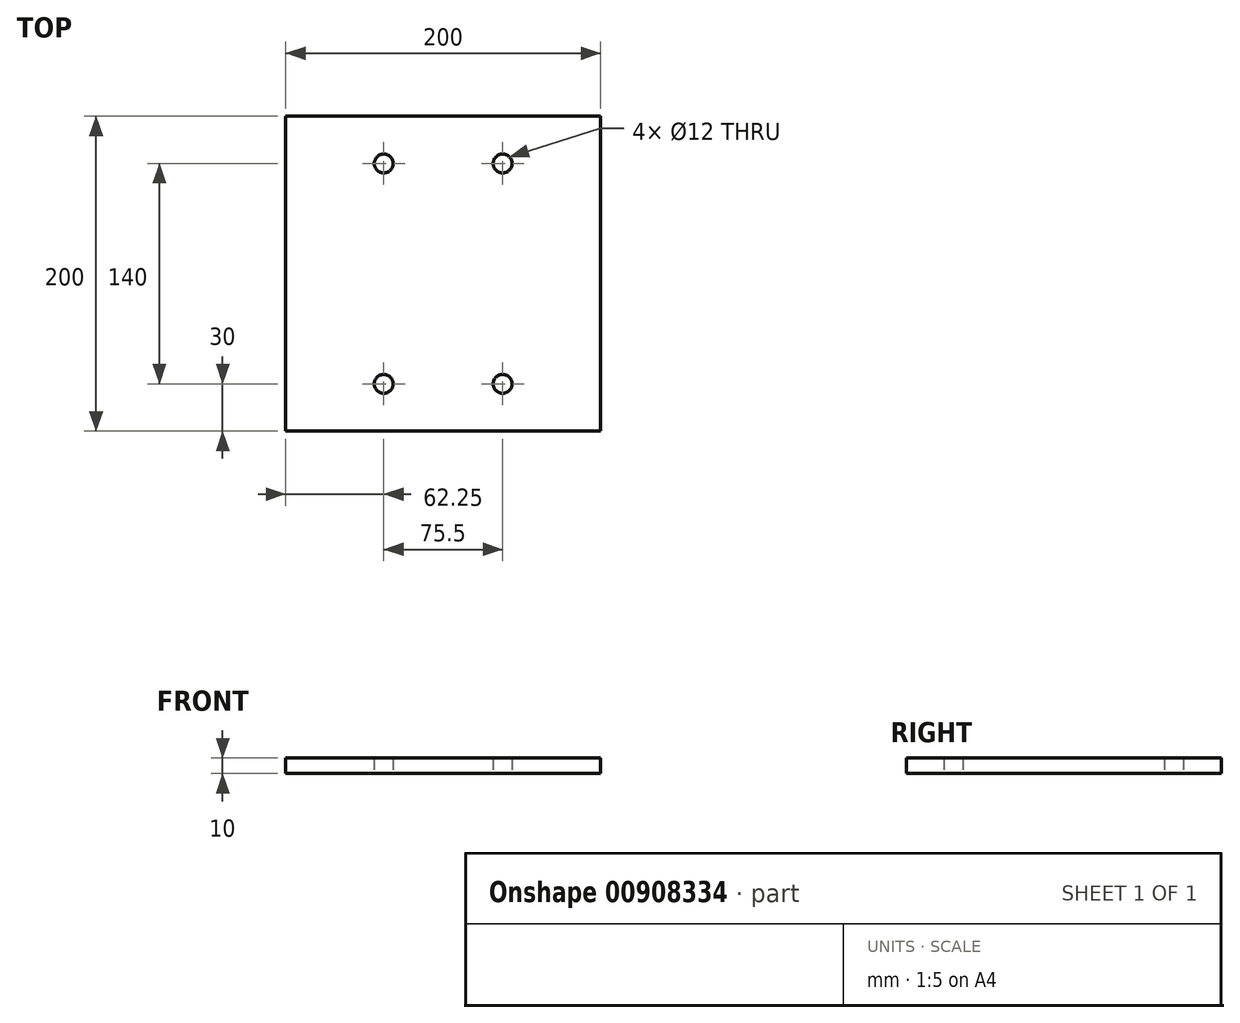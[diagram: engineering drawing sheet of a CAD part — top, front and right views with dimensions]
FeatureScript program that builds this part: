
annotation { "Feature Type Name" : "Feature", "Feature Type Description" : "" }
export const myFeature = defineFeature(function(context is Context, id is Id, definition is map)
    precondition{}
    {
        {
            var Q0;
            Q0=qCreatedBy(makeId("Top.planeOp"),FACE);
            var sketch = newSketch(context, id + "F0", { "sketchPlane" : qUnion([Q0])});
            skLineSegment(sketch, "E0.bottom", {"start": v(100, 100) * mm, "end": v(-100, 100) * mm});
            skLineSegment(sketch, "E0.top", {"start": v(100, -100) * mm, "end": v(-100, -100) * mm});
            skLineSegment(sketch, "E0.left", {"start": v(100, 100) * mm, "end": v(100, -100) * mm});
            skLineSegment(sketch, "E0.right", {"start": v(-100, 100) * mm, "end": v(-100, -100) * mm});
            skPoint(sketch, "E0.middle", {"position": v(0, 0) * mm});
            skCircle(sketch, "E1", {"center": v(-37.75, -70) * mm, "radius": 6 * mm});
            skCircle(sketch, "E2", {"center": v(37.75, -70) * mm, "radius": 6 * mm});
            skCircle(sketch, "E3", {"center": v(37.75, 70) * mm, "radius": 6 * mm});
            skCircle(sketch, "E4", {"center": v(-37.75, 70) * mm, "radius": 6 * mm});
            skSolve(sketch);
        }
        {
            var Q0;
            Q0=makeQuery(id+"F0.imprint","IMPRINT",FACE,{"disambiguationData":[TD([[makeQuery(id+"F0.imprint","IMPRINT",EDGE,{"derivedFrom":sQuery(id+"F0.wireOp",EDGE,"E0.bottom")}),1.0]])]});
            extrude(context, id + "F1", {"entities" : qUnion([Q0]), "depth" : 10 * mm, "offsetDistance" : 25 * mm});
        }
    });
